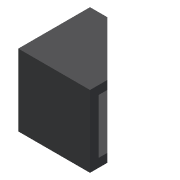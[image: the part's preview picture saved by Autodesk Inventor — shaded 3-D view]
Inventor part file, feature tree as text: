
AUTODESK INVENTOR PART (.ipt)
format: ipt  version: 2014 (Build 180170000, 170)  size: 83,456 bytes
history: native  units: mm
features: extrude x2, sketch x2
ambient origin geometry x8: Origin, YZ Plane, XZ Plane, XY Plane, X Axis, Y Axis, Z Axis, Center Point
bodies: Solid1 (feature_tree)
feature tree (4):
  extrude  "Extrusion1"  Depth=25.0mm
  extrude  "Extrusion2"  Depth=3.0mm
  sketch  "Sketch1"  dims[d0=25.0mm d1=6.0mm]
  sketch  "Sketch2"  dims[d2=25.0mm d3=0.0mm d4=3.0mm d5=3.0mm d6=3.0mm d7=22.0mm d8=0.0mm]
